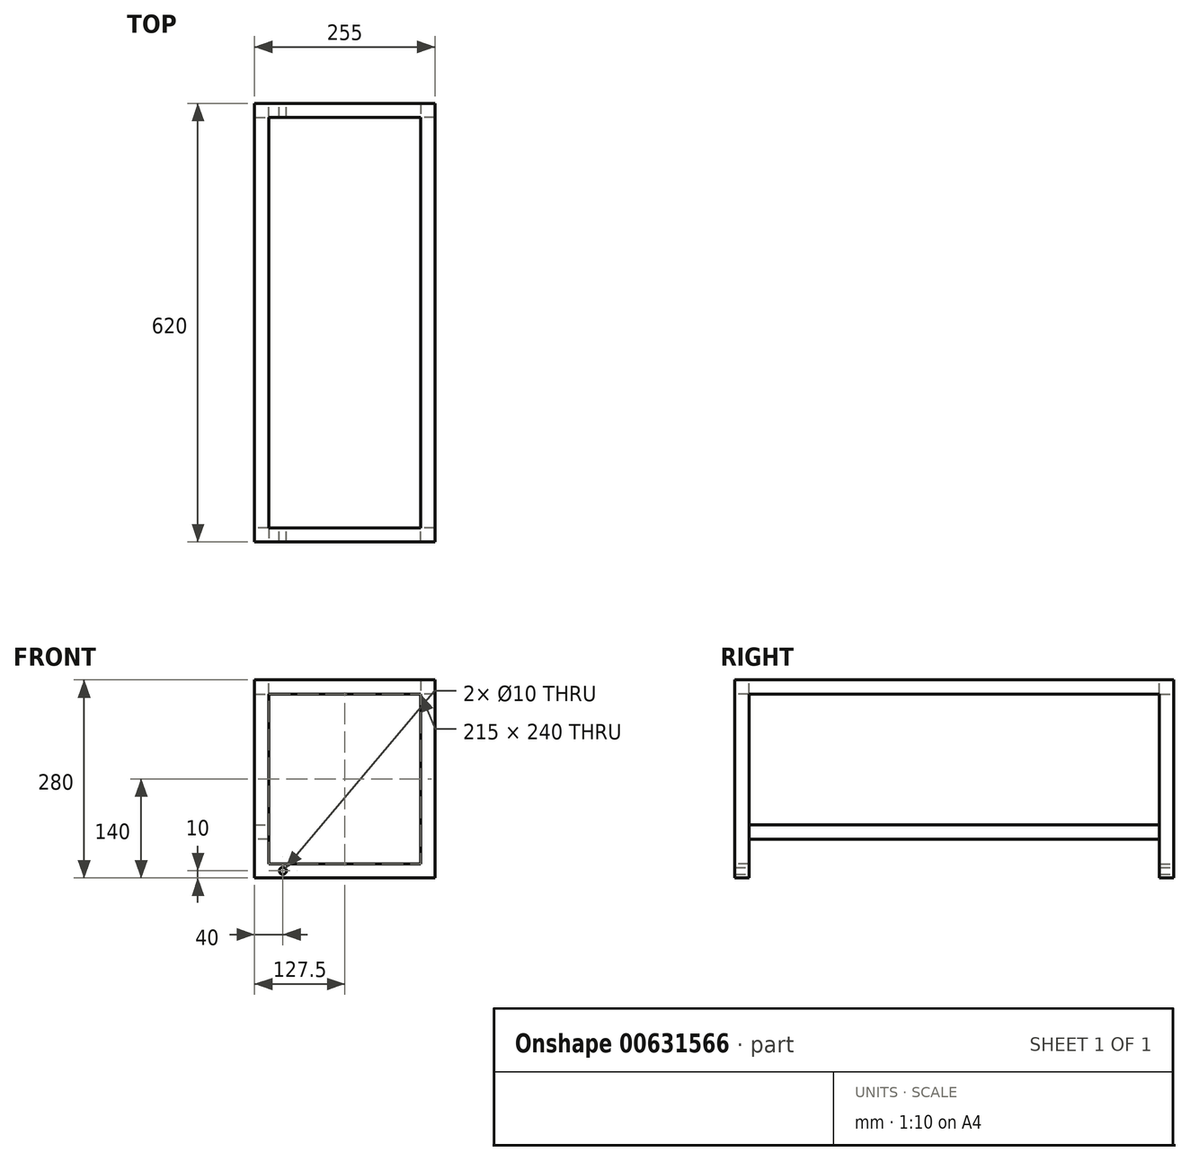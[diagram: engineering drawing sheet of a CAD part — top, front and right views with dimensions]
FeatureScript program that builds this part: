
annotation { "Feature Type Name" : "Feature", "Feature Type Description" : "" }
export const myFeature = defineFeature(function(context is Context, id is Id, definition is map)
    precondition{}
    {
        {
            var Q0;
            Q0=qCreatedBy(makeId("Front.planeOp"),FACE);
            var sketch = newSketch(context, id + "F0", { "sketchPlane" : qUnion([Q0])});
            skLineSegment(sketch, "E0.bottom", {"start": v(0, 270) * mm, "end": v(20, 270) * mm});
            skLineSegment(sketch, "E0.top", {"start": v(0, 250) * mm, "end": v(20, 250) * mm});
            skLineSegment(sketch, "E0.left", {"start": v(0, 270) * mm, "end": v(0, 250) * mm});
            skLineSegment(sketch, "E0.right", {"start": v(20, 270) * mm, "end": v(20, 250) * mm});
            skLineSegment(sketch, "E1.bottom", {"start": v(235, 270) * mm, "end": v(255, 270) * mm});
            skLineSegment(sketch, "E1.top", {"start": v(235, 250) * mm, "end": v(255, 250) * mm});
            skLineSegment(sketch, "E1.left", {"start": v(235, 270) * mm, "end": v(235, 250) * mm});
            skLineSegment(sketch, "E1.right", {"start": v(255, 270) * mm, "end": v(255, 250) * mm});
            skSolve(sketch);
        }
        {
            var Q0;
            Q0 = qSketchRegion(id + "F0", true);
            extrude(context, id + "F1", {"entities" : qUnion([Q0]), "depth" : 620 * mm, "offsetDistance" : 25 * mm, "symmetric" : true});
        }
        {
            var Q0;
            Q0=makeQuery(id+"F1.opExtrude","SWEPT_FACE",FACE,{"disambiguationData":[OSD([sQuery(id+"F0.wireOp",EDGE,"E0.top")])]});
            var sketch = newSketch(context, id + "F2", { "sketchPlane" : qUnion([Q0])});
            skLineSegment(sketch, "E2.bottom", {"start": v(0, 310) * mm, "end": v(20, 310) * mm});
            skLineSegment(sketch, "E2.top", {"start": v(0, 290) * mm, "end": v(20, 290) * mm});
            skLineSegment(sketch, "E2.left", {"start": v(0, 310) * mm, "end": v(0, 290) * mm});
            skLineSegment(sketch, "E2.right", {"start": v(20, 310) * mm, "end": v(20, 290) * mm});
            skLineSegment(sketch, "E3.bottom", {"start": v(0, -310) * mm, "end": v(20, -310) * mm});
            skLineSegment(sketch, "E3.top", {"start": v(0, -290) * mm, "end": v(20, -290) * mm});
            skLineSegment(sketch, "E3.left", {"start": v(0, -310) * mm, "end": v(0, -290) * mm});
            skLineSegment(sketch, "E3.right", {"start": v(20, -310) * mm, "end": v(20, -290) * mm});
            skLineSegment(sketch, "E4.bottom", {"start": v(255, -310) * mm, "end": v(235, -310) * mm});
            skLineSegment(sketch, "E4.top", {"start": v(255, -290) * mm, "end": v(235, -290) * mm});
            skLineSegment(sketch, "E4.left", {"start": v(255, -310) * mm, "end": v(255, -290) * mm});
            skLineSegment(sketch, "E4.right", {"start": v(235, -310) * mm, "end": v(235, -290) * mm});
            skLineSegment(sketch, "E5.bottom", {"start": v(255, 310) * mm, "end": v(235, 310) * mm});
            skLineSegment(sketch, "E5.top", {"start": v(255, 290) * mm, "end": v(235, 290) * mm});
            skLineSegment(sketch, "E5.left", {"start": v(255, 310) * mm, "end": v(255, 290) * mm});
            skLineSegment(sketch, "E5.right", {"start": v(235, 310) * mm, "end": v(235, 290) * mm});
            skSolve(sketch);
        }
        {
            var Q0;
            Q0 = qSketchRegion(id + "F2", true);
            extrude(context, id + "F3", {"entities" : qUnion([Q0]), "operationType" : NewBodyOperationType.ADD, "depth" : 260 * mm, "offsetDistance" : 25 * mm});
        }
        {
            var Q0;
            Q0=makeQuery(id+"F1.opExtrude","SWEPT_FACE",FACE,{"disambiguationData":[OSD([sQuery(id+"F0.wireOp",EDGE,"E1.left")])]});
            var sketch = newSketch(context, id + "F4", { "sketchPlane" : qUnion([Q0])});
            skLineSegment(sketch, "E6.bottom", {"start": v(-310, 270) * mm, "end": v(-290, 270) * mm});
            skLineSegment(sketch, "E6.top", {"start": v(-310, 250) * mm, "end": v(-290, 250) * mm});
            skLineSegment(sketch, "E6.left", {"start": v(-310, 270) * mm, "end": v(-310, 250) * mm});
            skLineSegment(sketch, "E6.right", {"start": v(-290, 270) * mm, "end": v(-290, 250) * mm});
            skLineSegment(sketch, "E7.bottom", {"start": v(-310, -10) * mm, "end": v(-290, -10) * mm});
            skLineSegment(sketch, "E7.top", {"start": v(-310, 10) * mm, "end": v(-290, 10) * mm});
            skLineSegment(sketch, "E7.left", {"start": v(-310, -10) * mm, "end": v(-310, 10) * mm});
            skLineSegment(sketch, "E7.right", {"start": v(-290, -10) * mm, "end": v(-290, 10) * mm});
            skLineSegment(sketch, "E8.bottom", {"start": v(310, -10) * mm, "end": v(290, -10) * mm});
            skLineSegment(sketch, "E8.top", {"start": v(310, 10) * mm, "end": v(290, 10) * mm});
            skLineSegment(sketch, "E8.left", {"start": v(310, -10) * mm, "end": v(310, 10) * mm});
            skLineSegment(sketch, "E8.right", {"start": v(290, -10) * mm, "end": v(290, 10) * mm});
            skLineSegment(sketch, "E9.bottom", {"start": v(310, 270) * mm, "end": v(290, 270) * mm});
            skLineSegment(sketch, "E9.top", {"start": v(310, 250) * mm, "end": v(290, 250) * mm});
            skLineSegment(sketch, "E9.left", {"start": v(310, 270) * mm, "end": v(310, 250) * mm});
            skLineSegment(sketch, "E9.right", {"start": v(290, 270) * mm, "end": v(290, 250) * mm});
            skSolve(sketch);
        }
        {
            var Q0;
            Q0 = qSketchRegion(id + "F4", true);
            var Q1;
            Q1=makeQuery(id+"F1.opExtrude","SWEPT_FACE",FACE,{"disambiguationData":[OSD([sQuery(id+"F0.wireOp",EDGE,"E0.right")])]});
            extrude(context, id + "F5", {"entities" : qUnion([Q0]), "operationType" : NewBodyOperationType.ADD, "endBound" : BoundingType.UP_TO_SURFACE, "depth" : 25 * mm, "endBoundEntityFace" : qUnion([Q1]), "offsetDistance" : 25 * mm});
        }
        {
            var Q0;
            Q0=makeQuery(id+"F3.opExtrude","SWEPT_FACE",FACE,{"disambiguationData":[OSD([sQuery(id+"F2.wireOp",EDGE,"E2.top")])]});
            var sketch = newSketch(context, id + "F6", { "sketchPlane" : qUnion([Q0])});
            skLineSegment(sketch, "E10.bottom", {"start": v(-20, 45) * mm, "end": v(0, 45) * mm});
            skLineSegment(sketch, "E10.top", {"start": v(-20, 65) * mm, "end": v(0, 65) * mm});
            skLineSegment(sketch, "E10.left", {"start": v(-20, 45) * mm, "end": v(-20, 65) * mm});
            skLineSegment(sketch, "E10.right", {"start": v(0, 45) * mm, "end": v(0, 65) * mm});
            skSolve(sketch);
        }
        {
            var Q0;
            Q0 = qSketchRegion(id + "F6", true);
            extrude(context, id + "F7", {"entities" : qUnion([Q0]), "operationType" : NewBodyOperationType.ADD, "endBound" : BoundingType.UP_TO_NEXT, "depth" : 25 * mm, "offsetDistance" : 25 * mm});
        }
        {
            var Q0;
            Q0=makeQuery(id+"F5.opExtrude","SWEPT_FACE",FACE,{"disambiguationData":[OSD([sQuery(id+"F4.wireOp",EDGE,"E7.left")])]});
            var sketch = newSketch(context, id + "F8", { "sketchPlane" : qUnion([Q0])});
            skCircle(sketch, "E11", {"center": v(-40, 0) * mm, "radius": 5 * mm});
            skSolve(sketch);
        }
        {
            var Q0;
            Q0 = qSketchRegion(id + "F8", true);
            var Q1;
            Q1=makeQuery(id+"F5.boolean.opBoolean","MERGE",FACE,{"derivedFrom":[makeQuery(id+"F3.boolean.opBoolean","MERGE",FACE,{"derivedFrom":[makeQuery(id+"F1.opExtrude","CAP_FACE",FACE,{"disambiguationData":[OSD([sQuery(id+"F0.wireOp",EDGE,"E0.bottom"),sQuery(id+"F0.wireOp",EDGE,"E0.top"),sQuery(id+"F0.wireOp",EDGE,"E0.left"),sQuery(id+"F0.wireOp",EDGE,"E0.right")])],"isStart":false}),makeQuery(id+"F3.opExtrude","SWEPT_FACE",FACE,{"disambiguationData":[OSD([sQuery(id+"F2.wireOp",EDGE,"E2.bottom")])]})]}),makeQuery(id+"F3.boolean.opBoolean","MERGE",FACE,{"derivedFrom":[makeQuery(id+"F1.opExtrude","CAP_FACE",FACE,{"disambiguationData":[OSD([sQuery(id+"F0.wireOp",EDGE,"E1.bottom"),sQuery(id+"F0.wireOp",EDGE,"E1.top"),sQuery(id+"F0.wireOp",EDGE,"E1.left"),sQuery(id+"F0.wireOp",EDGE,"E1.right")])],"isStart":false}),makeQuery(id+"F3.opExtrude","SWEPT_FACE",FACE,{"disambiguationData":[OSD([sQuery(id+"F2.wireOp",EDGE,"E5.bottom")])]})]}),makeQuery(id+"F5.opExtrude","SWEPT_FACE",FACE,{"disambiguationData":[OSD([sQuery(id+"F4.wireOp",EDGE,"E8.left")])]}),makeQuery(id+"F5.opExtrude","SWEPT_FACE",FACE,{"disambiguationData":[OSD([sQuery(id+"F4.wireOp",EDGE,"E9.left")])]})]});
            extrude(context, id + "F9", {"entities" : qUnion([Q0]), "operationType" : NewBodyOperationType.REMOVE, "endBound" : BoundingType.UP_TO_SURFACE, "oppositeDirection" : true, "depth" : 25 * mm, "endBoundEntityFace" : qUnion([Q1]), "offsetDistance" : 25 * mm});
        }
    });
